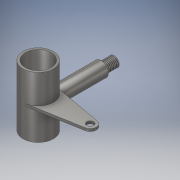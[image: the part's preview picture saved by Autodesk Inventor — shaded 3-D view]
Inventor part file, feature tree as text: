
AUTODESK INVENTOR PART (.ipt)
format: ipt  version: 2019 (Build 230136000, 136)  size: 182,272 bytes
history: native  units: mm
features: extrude x5, plane x3, sketch x3, thread x1, projected_geometry x1
ambient origin geometry x8: Origin, YZ Plane, XZ Plane, XY Plane, X Axis, Y Axis, Z Axis, Center Point
bodies: Solid1 (feature_tree)
feature tree (13):
  extrude  "Extrusion1"  Depth=30.0mm
  plane  "Work Plane5"
  plane  "Work Plane6"
  extrude  "Extrusion5"  Depth=9.599311mm
  plane  "Work Plane7"
  sketch  "Sketch8"  dims[d35=14.0mm d36=60.0mm d37=8.0mm d38=3.0mm d39=0.0mm d40=55.0mm d41=0.0mm d42=70.0mm d43=0.0mm d44=70.0mm d45=0.0mm d46=10.0mm d47=0.0mm]
  extrude  "Extrusion6"  Depth=10.0mm
  extrude  "Extrusion7"  Depth=10.0mm
  extrude  "Extrusion8"  Depth=10.0mm TaperAngle=0.0deg
  thread  "Thread2"  [1 undecoded]
  sketch  "Sketch1"  dims[d0=35.0mm d1=30.0mm]
  sketch  "Sketch7"  dims[d2=70.0mm d3=0.0mm d23=9.599311mm]
  projected_geometry  "Projected Loop4"
note: 1 required parameter value undecoded (feature->parameter linkage not recoverable at this tier; creation-order binding heuristic only, values carry confidence <= 0.55)
